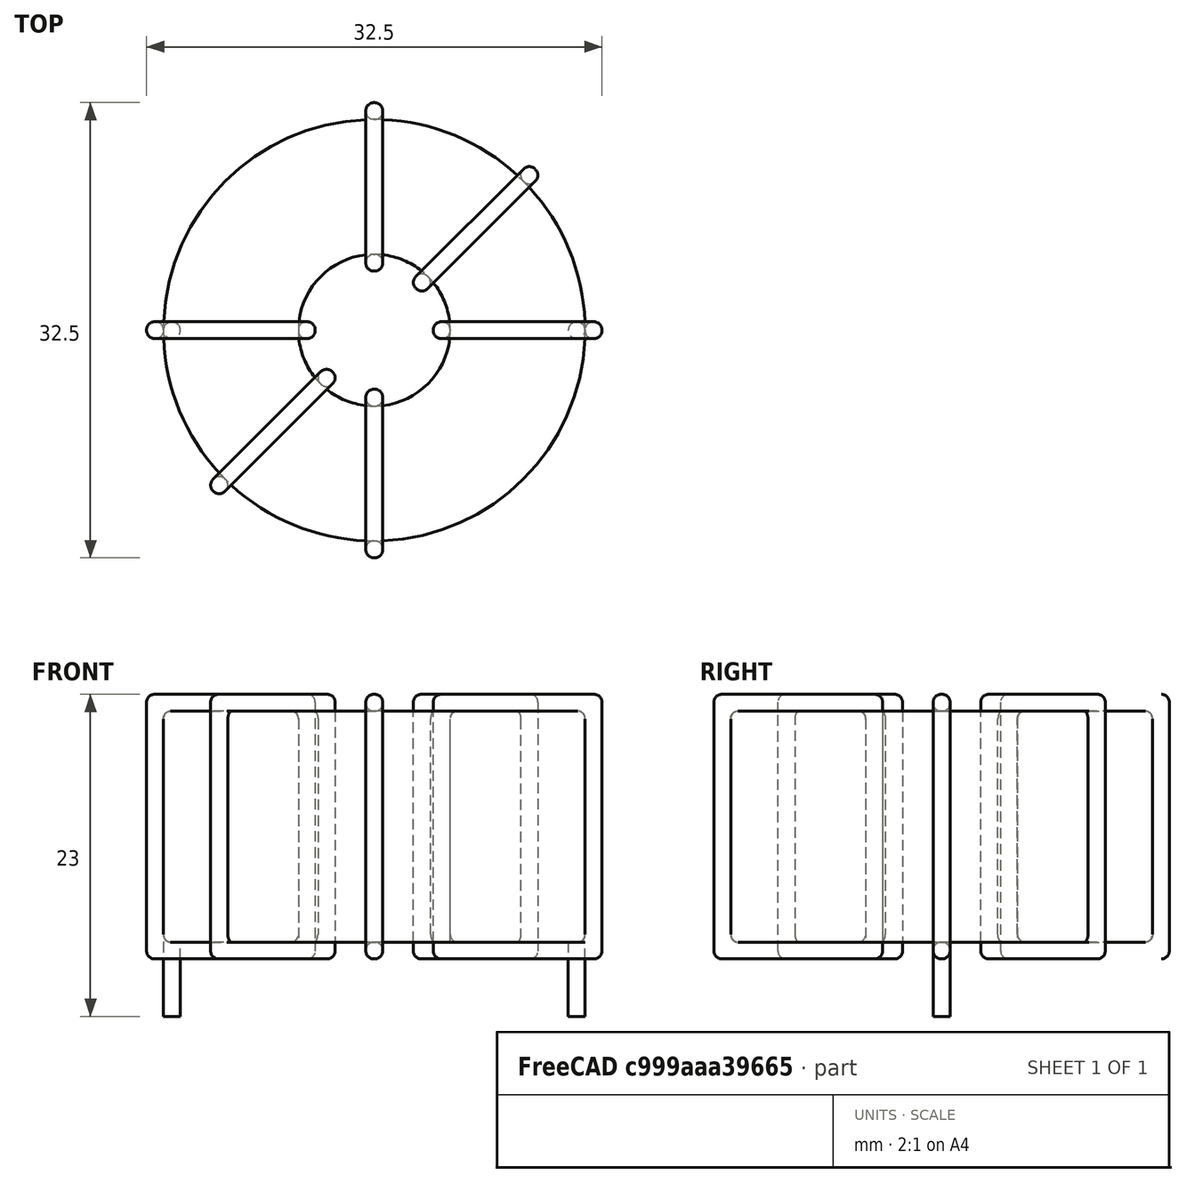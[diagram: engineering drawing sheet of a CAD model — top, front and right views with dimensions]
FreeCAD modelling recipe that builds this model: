
FCSTD DOCUMENT  (FreeCAD 0.16R6703 (Git))
Label: L_Toroid_Horizontal_D32.5mm_P28.90mm_Bourns_2300series
License: All rights reserved
LicenseURL: http://en.wikipedia.org/wiki/All_rights_reserved
objects: Sketcher::SketchObject×6, PartDesign::Pad×6, PartDesign::Fillet×5, Spreadsheet::Sheet×1
note: 23 computed .brp shape members not serialized (recipe doc carries the construction recipe); baked Part::Feature solids carry a one-line shape summary decoded from their .brp

FEATURE [Spreadsheet::Sheet] Spreadsheet  label="dimensions"
  cells = A1=Wx; B1(Wx)=32.5; C1(WW)=10.83333333333333; D1=32.5; A2=Wy; B2(Wy)=32.5; D2=32.5; A3=RM; B3(RMx)=28.9; C3(RMy)=0; A4=d_wire; B4(d_wire)=1.2; A5=H; B5(H)=16.5; A6=offsetx; B6(offsetx)=1.800000000000001
FEATURE [Sketcher::SketchObject] Sketch
  Placement = pos=(0,0,1.7) rot=(0,0,1;0rad)
  expr: Placement.Base.z = 0.5 + Spreadsheet.d_wire
  expr: Constraints[0] = Spreadsheet.Wx / 2 - Spreadsheet.d_wire
  expr: Constraints[4] = Spreadsheet.WW / 2
  expr: Constraints[2] = Spreadsheet.RMy / 2
  expr: Constraints[1] = Spreadsheet.RMx / 2
  sketch-geometry (2):
    g0: Circle CenterX=14.45 CenterY=0 CenterZ=0 NormalX=0 NormalY=0 NormalZ=1 Radius=15.05
    g1: Circle CenterX=14.45 CenterY=0 CenterZ=0 NormalX=0 NormalY=0 NormalZ=1 Radius=5.41667
  constraints (5):
    c: Radius(g0) = 15.05
    c: DistanceX(g-1,g0) = 14.45
    c: DistanceY(g-1,g0) = 0
    c: Coincident(g1,g0)
    c: Radius(g1) = 5.41667
FEATURE [PartDesign::Pad] Pad
  Length = 16.5
  Length2 = 100
  Placement = pos=(0,0,1.7) rot=(0,0,1;0rad)
  Sketch = -> Sketch
  Type = 0
  expr: Length = Spreadsheet.H
FEATURE [Sketcher::SketchObject] Sketch001
  Placement = pos=(0,0,1.1) rot=(0,0,1;0rad)
  expr: Placement.Base.z = 0.5 + Spreadsheet.d_wire * 0.5
  expr: Constraints[4] = Spreadsheet.RMx
  expr: Constraints[2] = Spreadsheet.RMy
  expr: Constraints[1] = Spreadsheet.d_wire / 2
  sketch-geometry (2):
    g0: Circle CenterX=0 CenterY=0 CenterZ=0 NormalX=0 NormalY=0 NormalZ=1 Radius=0.6
    g1: Circle CenterX=28.9 CenterY=0 CenterZ=0 NormalX=0 NormalY=0 NormalZ=1 Radius=0.6
  constraints (5):
    c: Equal(g0,g1)
    c: Radius(g0) = 0.6
    c: DistanceY(g-1,g1) = 0
    c: Coincident(g0,g-1)
    c: DistanceX(g-1,g1) = 28.9
FEATURE [PartDesign::Pad] Pad001
  Length = 0.6
  Length2 = 4.7
  Placement = pos=(0,0,1.1) rot=(0,0,1;0rad)
  Reversed = true
  Sketch = -> Sketch001
  Type = 4
  expr: Length2 = 3.5 + Spreadsheet.d_wire
  expr: Length = Spreadsheet.d_wire / 2
FEATURE [PartDesign::Fillet] Fillet
  Base = -> Pad [Edge6,Edge3,Edge2]
  Placement = pos=(0,0,1.7) rot=(0,0,1;0rad)
  Radius = 0.5
FEATURE [Sketcher::SketchObject] Sketch003
  Placement = pos=(14.45,0,0) rot=(1,0,0;1.5708rad)
  expr: Placement.Base.x = Spreadsheet.RMx / 2
  expr: Constraints[49] = Spreadsheet.Wx - Spreadsheet.d_wire * 2
  expr: Constraints[44] = Spreadsheet.d_wire
  expr: Constraints[23] = Spreadsheet.H
  expr: Constraints[22] = Spreadsheet.Wx / 2 - Spreadsheet.d_wire
  expr: Placement.Base.y = Spreadsheet.RMy / 2
  expr: Constraints[21] = (Spreadsheet.Wx - Spreadsheet.WW) / 2 - Spreadsheet.d_wire
  expr: Constraints[19] = Spreadsheet.d_wire
  expr: Constraints[17] = Spreadsheet.d_wire
  expr: Constraints[18] = Spreadsheet.d_wire
  expr: Constraints[16] = Spreadsheet.d_wire
  sketch-geometry (16):
    g0: LineSegment StartX=-4.21667 StartY=0.5 StartZ=0 EndX=-16.25 EndY=0.5 EndZ=0
    g1: LineSegment StartX=-16.25 StartY=0.5 StartZ=0 EndX=-16.25 EndY=19.4 EndZ=0
    g2: LineSegment StartX=-16.25 StartY=19.4 StartZ=0 EndX=-4.21667 EndY=19.4 EndZ=0
    g3: LineSegment StartX=-4.21667 StartY=19.4 StartZ=0 EndX=-4.21667 EndY=0.5 EndZ=0
    g4: LineSegment StartX=-15.05 StartY=18.2 StartZ=0 EndX=-5.41667 EndY=18.2 EndZ=0
    g5: LineSegment StartX=-5.41667 StartY=18.2 StartZ=0 EndX=-5.41667 EndY=1.7 EndZ=0
    g6: LineSegment StartX=-5.41667 StartY=1.7 StartZ=0 EndX=-15.05 EndY=1.7 EndZ=0
    g7: LineSegment StartX=-15.05 StartY=1.7 StartZ=0 EndX=-15.05 EndY=18.2 EndZ=0
    g8: LineSegment StartX=4.21667 StartY=19.4 StartZ=0 EndX=16.25 EndY=19.4 EndZ=0
    g9: LineSegment StartX=16.25 StartY=19.4 StartZ=0 EndX=16.25 EndY=0.5 EndZ=0
    g10: LineSegment StartX=16.25 StartY=0.5 StartZ=0 EndX=4.21667 EndY=0.5 EndZ=0
    g11: LineSegment StartX=4.21667 StartY=0.5 StartZ=0 EndX=4.21667 EndY=19.4 EndZ=0
    g12: LineSegment StartX=5.41667 StartY=18.2 StartZ=0 EndX=15.05 EndY=18.2 EndZ=0
    g13: LineSegment StartX=15.05 StartY=18.2 StartZ=0 EndX=15.05 EndY=1.7 EndZ=0
    g14: LineSegment StartX=15.05 StartY=1.7 StartZ=0 EndX=5.41667 EndY=1.7 EndZ=0
    g15: LineSegment StartX=5.41667 StartY=1.7 StartZ=0 EndX=5.41667 EndY=18.2 EndZ=0
  constraints (50):
    c: Horizontal(g0)
    c: Coincident(g1,g0)
    c: Vertical(g1)
    c: Coincident(g2,g1)
    c: Horizontal(g2)
    c: Coincident(g3,g2)
    c: Coincident(g3,g0)
    c: Vertical(g3)
    c: Coincident(g4,g5)
    c: Coincident(g5,g6)
    c: Coincident(g6,g7)
    c: Coincident(g7,g4)
    c: Horizontal(g4)
    c: Horizontal(g6)
    c: Vertical(g5)
    c: Vertical(g7)
    c: DistanceX(g1,g4) = 1.2
    c: DistanceY(g4,g1) = 1.2
    c: DistanceX(g5,g0) = 1.2
    c: DistanceY(g0,g5) = 1.2
    c: DistanceY(g-1,g0) = 0.5
    c: DistanceX(g6,g6) = 9.63333
    c: DistanceX(g6,g-1) = 15.05
    c: DistanceY(g7,g7) = 16.5
    c: Coincident(g8,g9)
    c: Coincident(g9,g10)
    c: Coincident(g10,g11)
    c: Coincident(g11,g8)
    c: Horizontal(g8)
    c: Horizontal(g10)
    c: Vertical(g9)
    c: Vertical(g11)
    c: Coincident(g12,g13)
    c: Coincident(g13,g14)
    c: Coincident(g14,g15)
    c: Coincident(g15,g12)
    c: Horizontal(g12)
    c: Horizontal(g14)
    c: Vertical(g13)
    c: Vertical(g15)
    c: DistanceY(g8,g2) = 0
    c: DistanceY(g10,g0) = 0
    c: DistanceY(g14,g5) = 0
    c: DistanceY(g12,g4) = 0
    c: DistanceX(g8,g12) = 1.2
    c: Equal(g8,g2)
    c: Equal(g12,g4)
    c: Equal(g9,g1)
    c: Equal(g13,g7)
    c: DistanceX(g4,g12) = 30.1
FEATURE [PartDesign::Pad] Pad002
  Length = 1.2
  Length2 = 100
  Midplane = true
  Placement = pos=(14.45,0,0) rot=(1,0,0;1.5708rad)
  Sketch = -> Sketch003
  Type = 0
  expr: Length = Spreadsheet.d_wire
FEATURE [PartDesign::Fillet] Fillet001
  Base = -> Pad002 [Edge38,Edge41,Edge42,Edge43,Edge29,Edge32,Edge33,Edge34,Edge25,Edge35,Edge36,Edge13,Edge14,Edge15,Edge16,Edge17,Edge18,Edge19,Edge1,Edge2,Edge3,Edge4,Edge5,Edge6,Edge7,Edge37,Edge39,Edge40,Edge20,Edge23,Edge24,Edge21,Edge22,Edge8,Edge9,Edge10,Edge11,Edge12,Edge26,Edge27,+8 more]
  Placement = pos=(14.45,0,0) rot=(1,0,0;1.5708rad)
  Radius = 0.564
  expr: Radius = Spreadsheet.d_wire * 0.47
FEATURE [Sketcher::SketchObject] Sketch004
  Placement = pos=(14.45,0,0) rot=(0.862856,0.357407,0.357407;1.71777rad)
  expr: Placement.Base.x = Spreadsheet.RMx / 2
  expr: Constraints[49] = Spreadsheet.Wx - 2 * Spreadsheet.d_wire
  expr: Constraints[44] = Spreadsheet.d_wire
  expr: Constraints[23] = Spreadsheet.H
  expr: Constraints[22] = Spreadsheet.Wx / 2 - Spreadsheet.d_wire
  expr: Placement.Base.y = Spreadsheet.RMy / 2
  expr: Constraints[21] = (Spreadsheet.Wx - Spreadsheet.WW) / 2 - Spreadsheet.d_wire
  expr: Constraints[19] = Spreadsheet.d_wire
  expr: Constraints[17] = Spreadsheet.d_wire
  expr: Constraints[18] = Spreadsheet.d_wire
  expr: Constraints[16] = Spreadsheet.d_wire
  sketch-geometry (16):
    g0: LineSegment StartX=-4.21667 StartY=0.5 StartZ=0 EndX=-16.25 EndY=0.5 EndZ=0
    g1: LineSegment StartX=-16.25 StartY=0.5 StartZ=0 EndX=-16.25 EndY=19.4 EndZ=0
    g2: LineSegment StartX=-16.25 StartY=19.4 StartZ=0 EndX=-4.21667 EndY=19.4 EndZ=0
    g3: LineSegment StartX=-4.21667 StartY=19.4 StartZ=0 EndX=-4.21667 EndY=0.5 EndZ=0
    g4: LineSegment StartX=-15.05 StartY=18.2 StartZ=0 EndX=-5.41667 EndY=18.2 EndZ=0
    g5: LineSegment StartX=-5.41667 StartY=18.2 StartZ=0 EndX=-5.41667 EndY=1.7 EndZ=0
    g6: LineSegment StartX=-5.41667 StartY=1.7 StartZ=0 EndX=-15.05 EndY=1.7 EndZ=0
    g7: LineSegment StartX=-15.05 StartY=1.7 StartZ=0 EndX=-15.05 EndY=18.2 EndZ=0
    g8: LineSegment StartX=4.21667 StartY=19.4 StartZ=0 EndX=16.25 EndY=19.4 EndZ=0
    g9: LineSegment StartX=16.25 StartY=19.4 StartZ=0 EndX=16.25 EndY=0.5 EndZ=0
    g10: LineSegment StartX=16.25 StartY=0.5 StartZ=0 EndX=4.21667 EndY=0.5 EndZ=0
    g11: LineSegment StartX=4.21667 StartY=0.5 StartZ=0 EndX=4.21667 EndY=19.4 EndZ=0
    g12: LineSegment StartX=5.41667 StartY=18.2 StartZ=0 EndX=15.05 EndY=18.2 EndZ=0
    g13: LineSegment StartX=15.05 StartY=18.2 StartZ=0 EndX=15.05 EndY=1.7 EndZ=0
    g14: LineSegment StartX=15.05 StartY=1.7 StartZ=0 EndX=5.41667 EndY=1.7 EndZ=0
    g15: LineSegment StartX=5.41667 StartY=1.7 StartZ=0 EndX=5.41667 EndY=18.2 EndZ=0
  constraints (50):
    c: Horizontal(g0)
    c: Coincident(g1,g0)
    c: Vertical(g1)
    c: Coincident(g2,g1)
    c: Horizontal(g2)
    c: Coincident(g3,g2)
    c: Coincident(g3,g0)
    c: Vertical(g3)
    c: Coincident(g4,g5)
    c: Coincident(g5,g6)
    c: Coincident(g6,g7)
    c: Coincident(g7,g4)
    c: Horizontal(g4)
    c: Horizontal(g6)
    c: Vertical(g5)
    c: Vertical(g7)
    c: DistanceX(g1,g4) = 1.2
    c: DistanceY(g4,g1) = 1.2
    c: DistanceX(g5,g0) = 1.2
    c: DistanceY(g0,g5) = 1.2
    c: DistanceY(g-1,g0) = 0.5
    c: DistanceX(g6,g6) = 9.63333
    c: DistanceX(g6,g-1) = 15.05
    c: DistanceY(g7,g7) = 16.5
    c: Coincident(g8,g9)
    c: Coincident(g9,g10)
    c: Coincident(g10,g11)
    c: Coincident(g11,g8)
    c: Horizontal(g8)
    c: Horizontal(g10)
    c: Vertical(g9)
    c: Vertical(g11)
    c: Coincident(g12,g13)
    c: Coincident(g13,g14)
    c: Coincident(g14,g15)
    c: Coincident(g15,g12)
    c: Horizontal(g12)
    c: Horizontal(g14)
    c: Vertical(g13)
    c: Vertical(g15)
    c: DistanceY(g8,g2) = 0
    c: DistanceY(g10,g0) = 0
    c: DistanceY(g14,g5) = 0
    c: DistanceY(g12,g4) = 0
    c: DistanceX(g8,g12) = 1.2
    c: Equal(g8,g2)
    c: Equal(g12,g4)
    c: Equal(g9,g1)
    c: Equal(g13,g7)
    c: DistanceX(g4,g12) = 30.1
FEATURE [PartDesign::Pad] Pad003
  Length = 1.2
  Length2 = 100
  Midplane = true
  Placement = pos=(14.45,0,0) rot=(0.862856,0.357407,0.357407;1.71777rad)
  Sketch = -> Sketch004
  Type = 0
  expr: Length = Spreadsheet.d_wire
FEATURE [PartDesign::Fillet] Fillet002
  Base = -> Pad003 [Edge38,Edge41,Edge42,Edge43,Edge29,Edge32,Edge33,Edge34,Edge25,Edge35,Edge36,Edge13,Edge14,Edge15,Edge16,Edge17,Edge18,Edge19,Edge1,Edge2,Edge3,Edge4,Edge5,Edge6,Edge7,Edge37,Edge39,Edge40,Edge20,Edge23,Edge24,Edge21,Edge22,Edge8,Edge9,Edge10,Edge11,Edge12,Edge26,Edge27,+8 more]
  Placement = pos=(14.45,0,0) rot=(0.862856,0.357407,0.357407;1.71777rad)
  Radius = 0.564
  expr: Radius = Spreadsheet.d_wire * 0.47
FEATURE [Sketcher::SketchObject] Sketch005
  Placement = pos=(14.45,0,0) rot=(0.862856,-0.357407,-0.357407;1.71777rad)
  expr: Placement.Base.x = Spreadsheet.RMx / 2
  expr: Constraints[49] = Spreadsheet.Wx - 2 * Spreadsheet.d_wire
  expr: Constraints[44] = Spreadsheet.d_wire
  expr: Constraints[23] = Spreadsheet.H
  expr: Constraints[22] = Spreadsheet.Wx / 2 - Spreadsheet.d_wire
  expr: Placement.Base.y = Spreadsheet.RMy / 2
  expr: Constraints[21] = (Spreadsheet.Wx - Spreadsheet.WW) / 2 - Spreadsheet.d_wire
  expr: Constraints[19] = Spreadsheet.d_wire
  expr: Constraints[17] = Spreadsheet.d_wire
  expr: Constraints[18] = Spreadsheet.d_wire
  expr: Constraints[16] = Spreadsheet.d_wire
  sketch-geometry (16):
    g0: LineSegment StartX=-4.21667 StartY=0.5 StartZ=0 EndX=-16.25 EndY=0.5 EndZ=0
    g1: LineSegment StartX=-16.25 StartY=0.5 StartZ=0 EndX=-16.25 EndY=19.4 EndZ=0
    g2: LineSegment StartX=-16.25 StartY=19.4 StartZ=0 EndX=-4.21667 EndY=19.4 EndZ=0
    g3: LineSegment StartX=-4.21667 StartY=19.4 StartZ=0 EndX=-4.21667 EndY=0.5 EndZ=0
    g4: LineSegment StartX=-15.05 StartY=18.2 StartZ=0 EndX=-5.41667 EndY=18.2 EndZ=0
    g5: LineSegment StartX=-5.41667 StartY=18.2 StartZ=0 EndX=-5.41667 EndY=1.7 EndZ=0
    g6: LineSegment StartX=-5.41667 StartY=1.7 StartZ=0 EndX=-15.05 EndY=1.7 EndZ=0
    g7: LineSegment StartX=-15.05 StartY=1.7 StartZ=0 EndX=-15.05 EndY=18.2 EndZ=0
    g8: LineSegment StartX=4.21667 StartY=19.4 StartZ=0 EndX=16.25 EndY=19.4 EndZ=0
    g9: LineSegment StartX=16.25 StartY=19.4 StartZ=0 EndX=16.25 EndY=0.5 EndZ=0
    g10: LineSegment StartX=16.25 StartY=0.5 StartZ=0 EndX=4.21667 EndY=0.5 EndZ=0
    g11: LineSegment StartX=4.21667 StartY=0.5 StartZ=0 EndX=4.21667 EndY=19.4 EndZ=0
    g12: LineSegment StartX=5.41667 StartY=18.2 StartZ=0 EndX=15.05 EndY=18.2 EndZ=0
    g13: LineSegment StartX=15.05 StartY=18.2 StartZ=0 EndX=15.05 EndY=1.7 EndZ=0
    g14: LineSegment StartX=15.05 StartY=1.7 StartZ=0 EndX=5.41667 EndY=1.7 EndZ=0
    g15: LineSegment StartX=5.41667 StartY=1.7 StartZ=0 EndX=5.41667 EndY=18.2 EndZ=0
  constraints (50):
    c: Horizontal(g0)
    c: Coincident(g1,g0)
    c: Vertical(g1)
    c: Coincident(g2,g1)
    c: Horizontal(g2)
    c: Coincident(g3,g2)
    c: Coincident(g3,g0)
    c: Vertical(g3)
    c: Coincident(g4,g5)
    c: Coincident(g5,g6)
    c: Coincident(g6,g7)
    c: Coincident(g7,g4)
    c: Horizontal(g4)
    c: Horizontal(g6)
    c: Vertical(g5)
    c: Vertical(g7)
    c: DistanceX(g1,g4) = 1.2
    c: DistanceY(g4,g1) = 1.2
    c: DistanceX(g5,g0) = 1.2
    c: DistanceY(g0,g5) = 1.2
    c: DistanceY(g-1,g0) = 0.5
    c: DistanceX(g6,g6) = 9.63333
    c: DistanceX(g6,g-1) = 15.05
    c: DistanceY(g7,g7) = 16.5
    c: Coincident(g8,g9)
    c: Coincident(g9,g10)
    c: Coincident(g10,g11)
    c: Coincident(g11,g8)
    c: Horizontal(g8)
    c: Horizontal(g10)
    c: Vertical(g9)
    c: Vertical(g11)
    c: Coincident(g12,g13)
    c: Coincident(g13,g14)
    c: Coincident(g14,g15)
    c: Coincident(g15,g12)
    c: Horizontal(g12)
    c: Horizontal(g14)
    c: Vertical(g13)
    c: Vertical(g15)
    c: DistanceY(g8,g2) = 0
    c: DistanceY(g10,g0) = 0
    c: DistanceY(g14,g5) = 0
    c: DistanceY(g12,g4) = 0
    c: DistanceX(g8,g12) = 1.2
    c: Equal(g8,g2)
    c: Equal(g12,g4)
    c: Equal(g9,g1)
    c: Equal(g13,g7)
    c: DistanceX(g4,g12) = 30.1
FEATURE [PartDesign::Pad] Pad004
  Length = 1.2
  Length2 = 100
  Midplane = true
  Placement = pos=(14.45,0,0) rot=(0.862856,-0.357407,-0.357407;1.71777rad)
  Sketch = -> Sketch005
  Type = 0
  expr: Length = Spreadsheet.d_wire
FEATURE [PartDesign::Fillet] Fillet003
  Base = -> Pad004 [Edge38,Edge41,Edge42,Edge43,Edge29,Edge32,Edge33,Edge34,Edge25,Edge35,Edge36,Edge13,Edge14,Edge15,Edge16,Edge17,Edge18,Edge19,Edge1,Edge2,Edge3,Edge4,Edge5,Edge6,Edge7,Edge37,Edge39,Edge40,Edge20,Edge23,Edge24,Edge21,Edge22,Edge8,Edge9,Edge10,Edge11,Edge12,Edge26,Edge27,+8 more]
  Placement = pos=(14.45,0,0) rot=(0.862856,-0.357407,-0.357407;1.71777rad)
  Radius = 0.564
  expr: Radius = Spreadsheet.d_wire * 0.47
FEATURE [Sketcher::SketchObject] Sketch006
  Placement = pos=(14.45,0,0) rot=(0.57735,0.57735,0.57735;2.0944rad)
  expr: Placement.Base.x = Spreadsheet.RMx / 2
  expr: Constraints[49] = Spreadsheet.Wx - Spreadsheet.d_wire * 2
  expr: Constraints[44] = Spreadsheet.d_wire
  expr: Constraints[23] = Spreadsheet.H
  expr: Constraints[22] = Spreadsheet.Wx / 2 - Spreadsheet.d_wire
  expr: Placement.Base.y = Spreadsheet.RMy / 2
  expr: Constraints[21] = (Spreadsheet.Wx - Spreadsheet.WW) / 2 - Spreadsheet.d_wire
  expr: Constraints[19] = Spreadsheet.d_wire
  expr: Constraints[17] = Spreadsheet.d_wire
  expr: Constraints[18] = Spreadsheet.d_wire
  expr: Constraints[16] = Spreadsheet.d_wire
  sketch-geometry (16):
    g0: LineSegment StartX=-4.21667 StartY=0.5 StartZ=0 EndX=-16.25 EndY=0.5 EndZ=0
    g1: LineSegment StartX=-16.25 StartY=0.5 StartZ=0 EndX=-16.25 EndY=19.4 EndZ=0
    g2: LineSegment StartX=-16.25 StartY=19.4 StartZ=0 EndX=-4.21667 EndY=19.4 EndZ=0
    g3: LineSegment StartX=-4.21667 StartY=19.4 StartZ=0 EndX=-4.21667 EndY=0.5 EndZ=0
    g4: LineSegment StartX=-15.05 StartY=18.2 StartZ=0 EndX=-5.41667 EndY=18.2 EndZ=0
    g5: LineSegment StartX=-5.41667 StartY=18.2 StartZ=0 EndX=-5.41667 EndY=1.7 EndZ=0
    g6: LineSegment StartX=-5.41667 StartY=1.7 StartZ=0 EndX=-15.05 EndY=1.7 EndZ=0
    g7: LineSegment StartX=-15.05 StartY=1.7 StartZ=0 EndX=-15.05 EndY=18.2 EndZ=0
    g8: LineSegment StartX=4.21667 StartY=19.4 StartZ=0 EndX=16.25 EndY=19.4 EndZ=0
    g9: LineSegment StartX=16.25 StartY=19.4 StartZ=0 EndX=16.25 EndY=0.5 EndZ=0
    g10: LineSegment StartX=16.25 StartY=0.5 StartZ=0 EndX=4.21667 EndY=0.5 EndZ=0
    g11: LineSegment StartX=4.21667 StartY=0.5 StartZ=0 EndX=4.21667 EndY=19.4 EndZ=0
    g12: LineSegment StartX=5.41667 StartY=18.2 StartZ=0 EndX=15.05 EndY=18.2 EndZ=0
    g13: LineSegment StartX=15.05 StartY=18.2 StartZ=0 EndX=15.05 EndY=1.7 EndZ=0
    g14: LineSegment StartX=15.05 StartY=1.7 StartZ=0 EndX=5.41667 EndY=1.7 EndZ=0
    g15: LineSegment StartX=5.41667 StartY=1.7 StartZ=0 EndX=5.41667 EndY=18.2 EndZ=0
  constraints (50):
    c: Horizontal(g0)
    c: Coincident(g1,g0)
    c: Vertical(g1)
    c: Coincident(g2,g1)
    c: Horizontal(g2)
    c: Coincident(g3,g2)
    c: Coincident(g3,g0)
    c: Vertical(g3)
    c: Coincident(g4,g5)
    c: Coincident(g5,g6)
    c: Coincident(g6,g7)
    c: Coincident(g7,g4)
    c: Horizontal(g4)
    c: Horizontal(g6)
    c: Vertical(g5)
    c: Vertical(g7)
    c: DistanceX(g1,g4) = 1.2
    c: DistanceY(g4,g1) = 1.2
    c: DistanceX(g5,g0) = 1.2
    c: DistanceY(g0,g5) = 1.2
    c: DistanceY(g-1,g0) = 0.5
    c: DistanceX(g6,g6) = 9.63333
    c: DistanceX(g6,g-1) = 15.05
    c: DistanceY(g7,g7) = 16.5
    c: Coincident(g8,g9)
    c: Coincident(g9,g10)
    c: Coincident(g10,g11)
    c: Coincident(g11,g8)
    c: Horizontal(g8)
    c: Horizontal(g10)
    c: Vertical(g9)
    c: Vertical(g11)
    c: Coincident(g12,g13)
    c: Coincident(g13,g14)
    c: Coincident(g14,g15)
    c: Coincident(g15,g12)
    c: Horizontal(g12)
    c: Horizontal(g14)
    c: Vertical(g13)
    c: Vertical(g15)
    c: DistanceY(g8,g2) = 0
    c: DistanceY(g10,g0) = 0
    c: DistanceY(g14,g5) = 0
    c: DistanceY(g12,g4) = 0
    c: DistanceX(g8,g12) = 1.2
    c: Equal(g8,g2)
    c: Equal(g12,g4)
    c: Equal(g9,g1)
    c: Equal(g13,g7)
    c: DistanceX(g4,g12) = 30.1
FEATURE [PartDesign::Pad] Pad005
  Length = 1.2
  Length2 = 100
  Midplane = true
  Placement = pos=(14.45,0,0) rot=(0.57735,0.57735,0.57735;2.0944rad)
  Sketch = -> Sketch006
  Type = 0
  expr: Length = Spreadsheet.d_wire
FEATURE [PartDesign::Fillet] Fillet004
  Base = -> Pad005 [Edge38,Edge41,Edge42,Edge43,Edge29,Edge32,Edge33,Edge34,Edge25,Edge35,Edge36,Edge13,Edge14,Edge15,Edge16,Edge17,Edge18,Edge19,Edge1,Edge2,Edge3,Edge4,Edge5,Edge6,Edge7,Edge37,Edge39,Edge40,Edge20,Edge23,Edge24,Edge21,Edge22,Edge8,Edge9,Edge10,Edge11,Edge12,Edge26,Edge27,+8 more]
  Placement = pos=(14.45,0,0) rot=(0.57735,0.57735,0.57735;2.0944rad)
  Radius = 0.564
  expr: Radius = Spreadsheet.d_wire * 0.47
